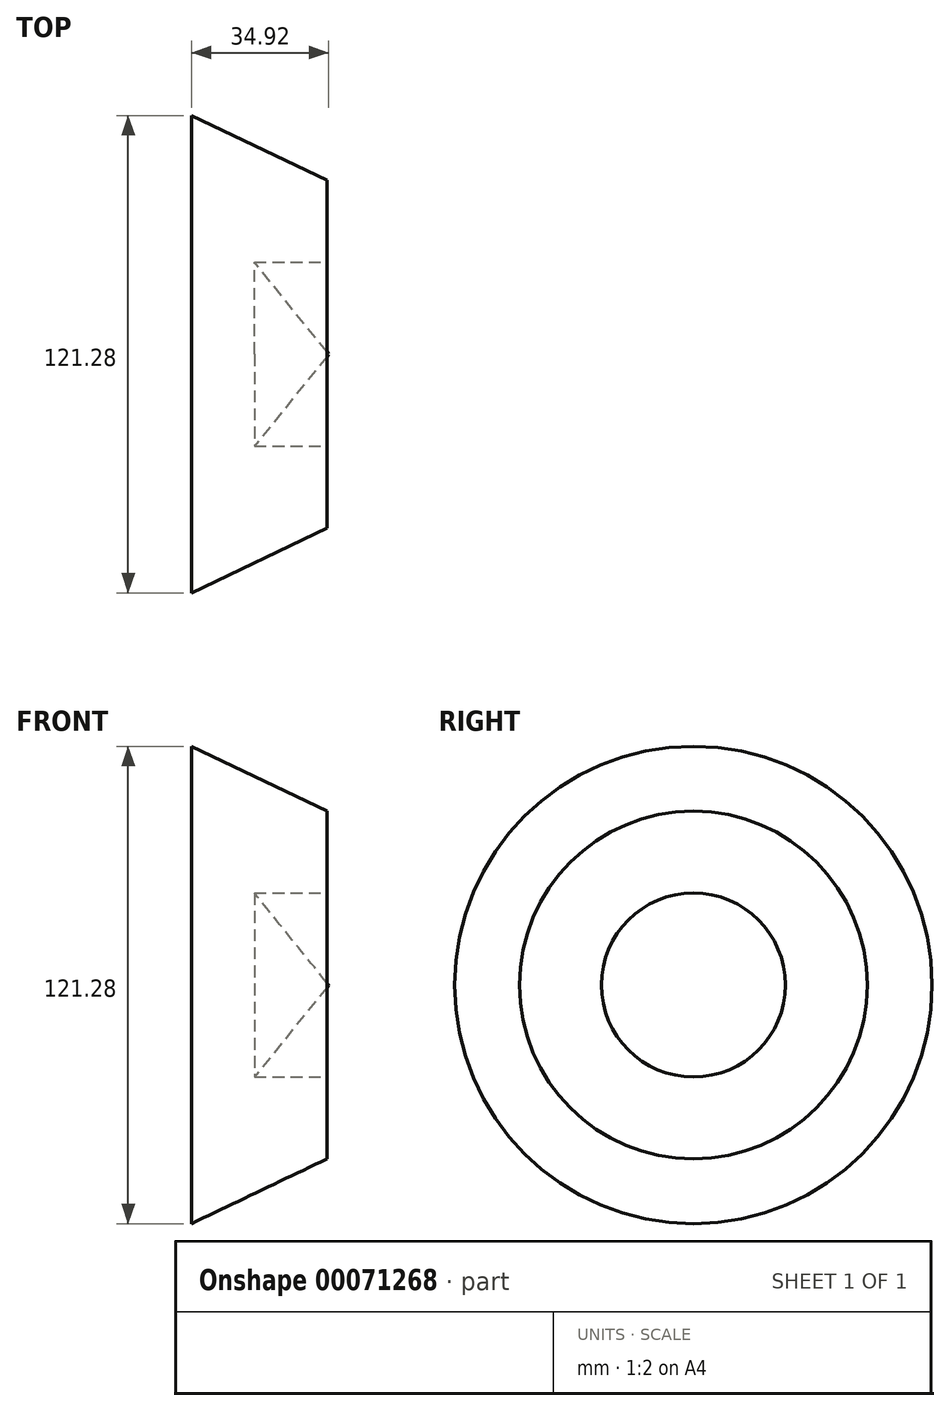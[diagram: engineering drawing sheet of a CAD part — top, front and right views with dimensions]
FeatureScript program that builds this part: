
annotation { "Feature Type Name" : "Feature", "Feature Type Description" : "" }
export const myFeature = defineFeature(function(context is Context, id is Id, definition is map)
    precondition{}
    {
        {
            var Q0;
            Q0=qCreatedBy(makeId("Top.planeOp"),FACE);
            var sketch = newSketch(context, id + "F0", { "sketchPlane" : qUnion([Q0])});
            skLineSegment(sketch, "E0", {"start": v(0, 0) * mm, "end": v(0, 60.64) * mm});
            skLineSegment(sketch, "E1", {"start": v(0, 60.64) * mm, "end": v(34.45, 44.18) * mm});
            skLineSegment(sketch, "E2", {"start": v(34.45, 44.18) * mm, "end": v(34.45, 23.36) * mm});
            skLineSegment(sketch, "E3", {"start": v(34.45, 23.36) * mm, "end": v(16.04, 23.36) * mm});
            skLineSegment(sketch, "E4", {"start": v(16.04, 23.36) * mm, "end": v(34.92, 0) * mm});
            skLineSegment(sketch, "E5", {"start": v(34.92, 0) * mm, "end": v(0, 0) * mm});
            skSolve(sketch);
        }
        {
            var Q0;
            Q0=makeQuery(id+"F0.imprint","IMPRINT",FACE,{"disambiguationData":[TD([[makeQuery(id+"F0.imprint","IMPRINT",EDGE,{"derivedFrom":sQuery(id+"F0.wireOp",EDGE,"E0")}),-1.0]])]});
            var Q1;
            Q1=sQuery(id+"F0.wireOp",EDGE,"E5");
            revolve(context, id + "F1", {"entities" : qUnion([Q0]), "axis" : qUnion([Q1]), "revolveType" : RevolveType.FULL});
        }
    });
